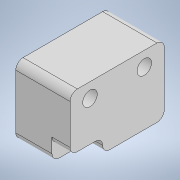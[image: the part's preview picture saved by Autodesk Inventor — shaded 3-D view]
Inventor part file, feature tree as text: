
AUTODESK INVENTOR PART (.ipt)
format: ipt  version: 2022 (Build 260153000, 153)  size: 126,464 bytes
history: native  units: mm
features: extrude x3, sketch x3, fillet x1
ambient origin geometry x8: Origin, YZ Plane, XZ Plane, XY Plane, X Axis, Y Axis, Z Axis, Center Point
bodies: Solid1 (feature_tree)
feature tree (7):
  extrude  "Extrusion1"  Depth=26.0mm
  extrude  "Extrusion2"  Depth=15.0mm
  extrude  "Extrusion3"  TaperAngle=0.0deg  [1 undecoded]
  fillet  "Fillet1"  Radius=4.0mm
  sketch  "Sketch1"  dims[d0=15.0mm d1=26.0mm]
  sketch  "Sketch2"  dims[d2=19.0mm d3=0.0mm d4=15.0mm]
  sketch  "Sketch3"  dims[d5=15.0mm d6=0.0mm d7=0.0mm d8=4.0mm d9=9.0mm d10=5.0mm d11=0.0mm d12=2.0mm]
note: 1 required parameter value undecoded (feature->parameter linkage not recoverable at this tier; creation-order binding heuristic only, values carry confidence <= 0.55)
